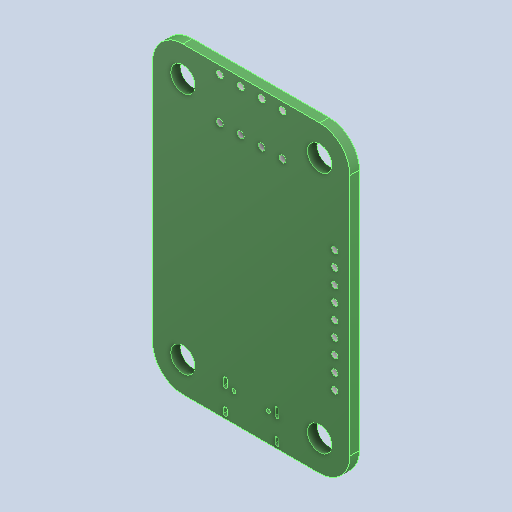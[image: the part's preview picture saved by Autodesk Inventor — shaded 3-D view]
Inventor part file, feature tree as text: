
AUTODESK INVENTOR PART (.ipt)
format: ipt  version: 2022.3 (Build 263350000, 350)  size: 145,920 bytes
history: native  units: in
note: dims shown in document units (in); Inventor stores cm internally (conversion verified against a paired STEP export)
features: fillet x1
ambient origin geometry x8: Origin, YZ Plane, XZ Plane, XY Plane, X Axis, Y Axis, Z Axis, Center Point
bodies: Solid1 (feature_tree)
feature tree (1):
  fillet  "Fillet1"  [1 undecoded]
note: 1 required parameter value undecoded (feature->parameter linkage not recoverable at this tier; creation-order binding heuristic only, values carry confidence <= 0.55)
